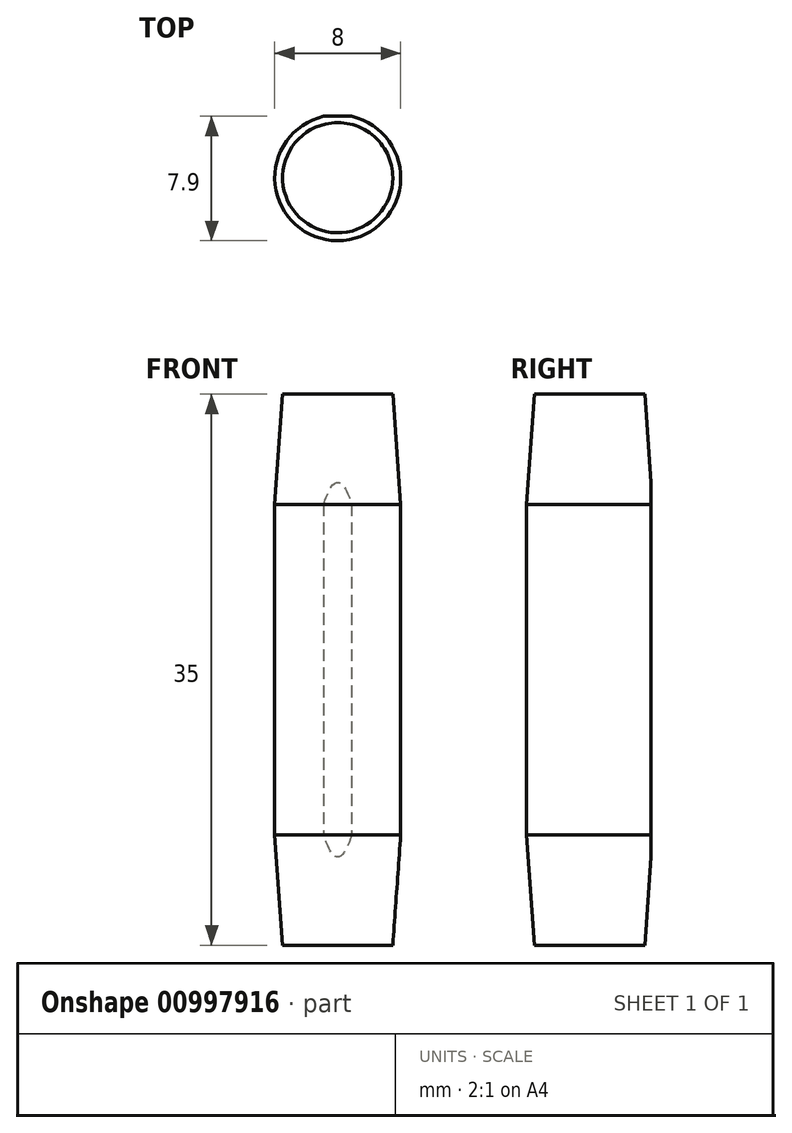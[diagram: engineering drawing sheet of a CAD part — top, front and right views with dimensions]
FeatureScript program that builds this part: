
annotation { "Feature Type Name" : "Feature", "Feature Type Description" : "" }
export const myFeature = defineFeature(function(context is Context, id is Id, definition is map)
    precondition{}
    {
        {
            var Q0;
            Q0=qCreatedBy(makeId("Top.planeOp"),FACE);
            var sketch = newSketch(context, id + "F0", { "sketchPlane" : qUnion([Q0])});
            skCircle(sketch, "E0", {"center": v(0, 0) * mm, "radius": 4 * mm});
            skSolve(sketch);
        }
        {
            var Q0;
            Q0 = qSketchRegion(id + "F0", true);
            extrude(context, id + "F1", {"entities" : qUnion([Q0]), "depth" : 35 * mm, "offsetDistance" : 25 * mm});
        }
        {
            var Q0;
            Q0=makeQuery(id+"F1.opExtrude","CAP_EDGE",EDGE,{"disambiguationData":[OSD([sQuery(id+"F0.wireOp",EDGE,"E0")])],"isStart":false});
            var Q1;
            Q1=makeQuery(id+"F1.opExtrude","CAP_EDGE",EDGE,{"disambiguationData":[OSD([sQuery(id+"F0.wireOp",EDGE,"E0")])],"isStart":true});
            chamfer(context, id + "F2", {"entities" : qUnion([Q0, Q1]), "chamferType" : ChamferType.TWO_OFFSETS, "width1" : 0.5 * mm, "oppositeDirection" : false, "width2" : 7 * mm, "tangentPropagation" : true});
        }
        {
            var Q0;
            Q0=qCreatedBy(makeId("Right.planeOp"),FACE);
            var sketch = newSketch(context, id + "F3", { "sketchPlane" : qUnion([Q0])});
            skLineSegment(sketch, "E1.bottom", {"start": v(3.9, 35) * mm, "end": v(13.9, 35) * mm});
            skLineSegment(sketch, "E1.top", {"start": v(3.9, 0) * mm, "end": v(13.9, 0) * mm});
            skLineSegment(sketch, "E1.left", {"start": v(3.9, 35) * mm, "end": v(3.9, 0) * mm});
            skLineSegment(sketch, "E1.right", {"start": v(13.9, 35) * mm, "end": v(13.9, 0) * mm});
            skSolve(sketch);
        }
        {
            var Q0;
            Q0 = qSketchRegion(id + "F3", true);
            extrude(context, id + "F4", {"entities" : qUnion([Q0]), "operationType" : NewBodyOperationType.REMOVE, "endBound" : BoundingType.SYMMETRIC, "oppositeDirection" : true, "depth" : 25 * mm, "offsetDistance" : 25 * mm});
        }
    });
